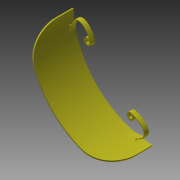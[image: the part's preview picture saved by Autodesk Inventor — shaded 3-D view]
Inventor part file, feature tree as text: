
AUTODESK INVENTOR PART (.ipt)
format: ipt  version: 2015 (Build 190159000, 159)  size: 372,736 bytes
history: native  units: mm
features: sketch x6, extrude x5, fillet x4, other x1
ambient origin geometry x8: Origin, YZ Plane, XZ Plane, XY Plane, X Axis, Y Axis, Z Axis, Center Point
bodies: Body1 (feature_tree)
feature tree (16):
  other  "Sólido1"
  extrude  "Extrusión1"  Depth=300.0mm
  sketch  "Boceto3"  dims[d2=270.0mm d3=10.0mm]
  extrude  "Extrusión3"  Depth=10.0mm
  extrude  "Extrusión4"  Depth=3.0mm
  sketch  "Boceto5"  dims[d7=0.5mm d8=35.0mm d9=3.0mm d10=0.5mm]
  extrude  "Extrusión5"  Depth=3.0mm
  fillet  "Empalme2"  Radius=3.0mm
  fillet  "Empalme3"  Radius=0.5mm
  sketch  "Boceto6"  dims[d11=6.0mm d12=35.0mm d14=8.0mm d15=0.0mm d19=1.5mm]
  sketch  "Boceto7"  dims[d20=1.5mm d23=135.0deg d27=0.174533mm d28=0.174533mm d29=8.0mm d30=0.0mm d31=8.0mm d32=0.0mm d33=40.0mm d34=0.0mm d35=1.0mm d36=5.0mm d40=460.0mm d42=360.0deg d44=80.0mm d45=0.0mm d49=50.0mm d51=3.0mm]
  extrude  "Extrusión6"  Depth=35.0mm
  fillet  "Empalme5"  Radius=8.0mm
  fillet  "Empalme7"  Radius=1.5mm
  sketch  "Boceto1"  dims[d0=292.0mm d1=300.0mm]
  sketch  "Boceto4"  dims[d4=6.0mm d6=3.0mm]
